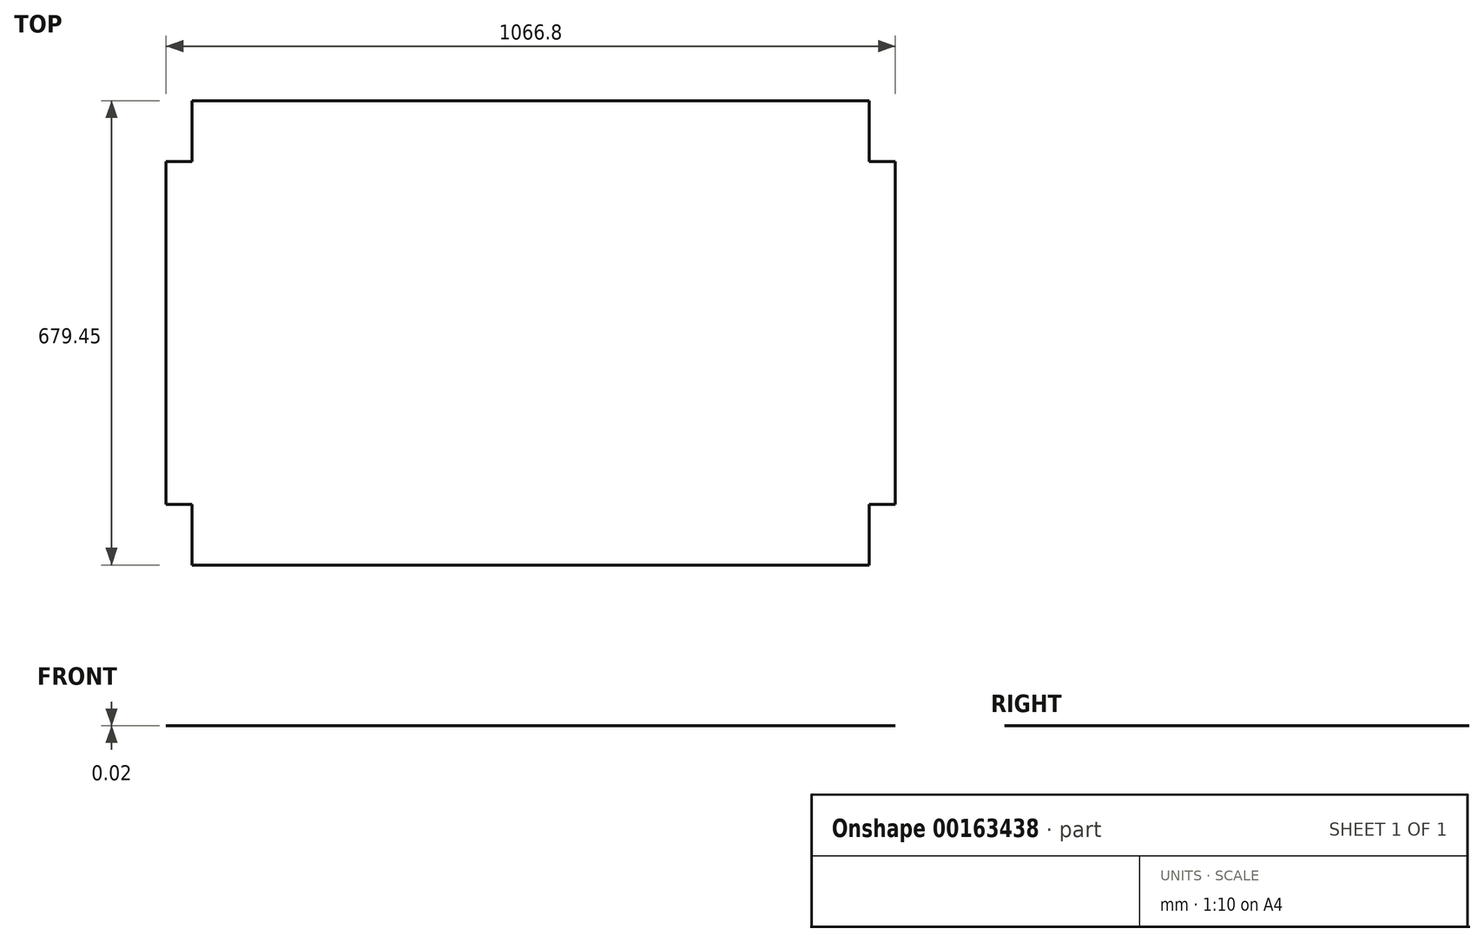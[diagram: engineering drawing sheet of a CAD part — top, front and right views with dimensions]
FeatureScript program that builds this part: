
annotation { "Feature Type Name" : "Feature", "Feature Type Description" : "" }
export const myFeature = defineFeature(function(context is Context, id is Id, definition is map)
    precondition{}
    {
        {
            var Q0;
            Q0=qCreatedBy(makeId("Top.planeOp"),FACE);
            var sketch = newSketch(context, id + "F0", { "sketchPlane" : qUnion([Q0])});
            skLineSegment(sketch, "E0.bottom", {"start": v(0, 0) * mm, "end": v(1066.8, 0) * mm});
            skLineSegment(sketch, "E0.top", {"start": v(0, 679.45) * mm, "end": v(1066.8, 679.45) * mm});
            skLineSegment(sketch, "E0.left", {"start": v(0, 0) * mm, "end": v(0, 679.45) * mm});
            skLineSegment(sketch, "E0.right", {"start": v(1066.8, 0) * mm, "end": v(1066.8, 679.45) * mm});
            skSolve(sketch);
        }
        {
            var Q0;
            Q0 = qSketchRegion(id + "F0", true);
            extrude(context, id + "F1", {"entities" : qUnion([Q0]), "depth" : 5 / 203.2 * mm});
        }
        {
            var Q0;
            Q0=makeQuery(id+"F1.opExtrude","CAP_FACE",FACE,{"disambiguationData":[OSD([sQuery(id+"F0.wireOp",EDGE,"E0.bottom"),sQuery(id+"F0.wireOp",EDGE,"E0.top"),sQuery(id+"F0.wireOp",EDGE,"E0.left"),sQuery(id+"F0.wireOp",EDGE,"E0.right")])],"isStart":false});
            var sketch = newSketch(context, id + "F2", { "sketchPlane" : qUnion([Q0])});
            skLineSegment(sketch, "E1.bottom", {"start": v(0, 679.45) * mm, "end": v(38.1, 679.45) * mm});
            skLineSegment(sketch, "E1.top", {"start": v(0, 590.55) * mm, "end": v(38.1, 590.55) * mm});
            skLineSegment(sketch, "E1.left", {"start": v(0, 679.45) * mm, "end": v(0, 590.55) * mm});
            skLineSegment(sketch, "E1.right", {"start": v(38.1, 679.45) * mm, "end": v(38.1, 590.55) * mm});
            skLineSegment(sketch, "E2", {"start": v(533.4, 679.45) * mm, "end": v(533.4, 339.73) * mm, "construction": true});
            skLineSegment(sketch, "E3", {"start": v(533.4, 339.73) * mm, "end": v(1066.8, 339.73) * mm, "construction": true});
            skLineSegment(sketch, "E4.MirrorCS", {"start": v(1028.7, 679.45) * mm, "end": v(1028.7, 590.55) * mm});
            skLineSegment(sketch, "E5.MirrorCS", {"start": v(1066.8, 679.45) * mm, "end": v(1066.8, 590.55) * mm});
            skLineSegment(sketch, "E6.MirrorCS", {"start": v(1066.8, 590.55) * mm, "end": v(1028.7, 590.55) * mm});
            skLineSegment(sketch, "E7.MirrorCS", {"start": v(1066.8, 679.45) * mm, "end": v(1028.7, 679.45) * mm});
            skLineSegment(sketch, "E8.MirrorCS", {"start": v(38.1, 0) * mm, "end": v(38.1, 88.9) * mm});
            skLineSegment(sketch, "E9.MirrorCS", {"start": v(0, 0) * mm, "end": v(0, 88.9) * mm});
            skLineSegment(sketch, "E10.MirrorCS", {"start": v(0, 88.9) * mm, "end": v(38.1, 88.9) * mm});
            skLineSegment(sketch, "E11.MirrorCS", {"start": v(0, 0) * mm, "end": v(38.1, 0) * mm});
            skLineSegment(sketch, "E12.MirrorCS", {"start": v(1028.7, 0) * mm, "end": v(1028.7, 88.9) * mm});
            skLineSegment(sketch, "E13.MirrorCS", {"start": v(1066.8, 0) * mm, "end": v(1066.8, 88.9) * mm});
            skLineSegment(sketch, "E14.MirrorCS", {"start": v(1066.8, 88.9) * mm, "end": v(1028.7, 88.9) * mm});
            skLineSegment(sketch, "E15.MirrorCS", {"start": v(1066.8, 0) * mm, "end": v(1028.7, 0) * mm});
            skSolve(sketch);
        }
        {
            var Q0;
            Q0=makeQuery(id+"F2.imprint","IMPRINT",FACE,{"disambiguationData":[TD([[makeQuery(id+"F2.imprint","IMPRINT",EDGE,{"derivedFrom":sQuery(id+"F2.wireOp",EDGE,"E8.MirrorCS")}),1.0]])]});
            var Q1;
            Q1=makeQuery(id+"F2.imprint","IMPRINT",FACE,{"disambiguationData":[TD([[makeQuery(id+"F2.imprint","IMPRINT",EDGE,{"derivedFrom":sQuery(id+"F2.wireOp",EDGE,"E1.bottom")}),-1.0]])]});
            var Q2;
            Q2=makeQuery(id+"F2.imprint","IMPRINT",FACE,{"disambiguationData":[TD([[makeQuery(id+"F2.imprint","IMPRINT",EDGE,{"derivedFrom":sQuery(id+"F2.wireOp",EDGE,"E4.MirrorCS")}),1.0]])]});
            var Q3;
            Q3=makeQuery(id+"F2.imprint","IMPRINT",FACE,{"disambiguationData":[TD([[makeQuery(id+"F2.imprint","IMPRINT",EDGE,{"derivedFrom":sQuery(id+"F2.wireOp",EDGE,"E12.MirrorCS")}),-1.0]])]});
            extrude(context, id + "F3", {"entities" : qUnion([Q0, Q1, Q2, Q3]), "operationType" : NewBodyOperationType.REMOVE, "oppositeDirection" : true, "depth" : 25.4 * mm});
        }
    });
